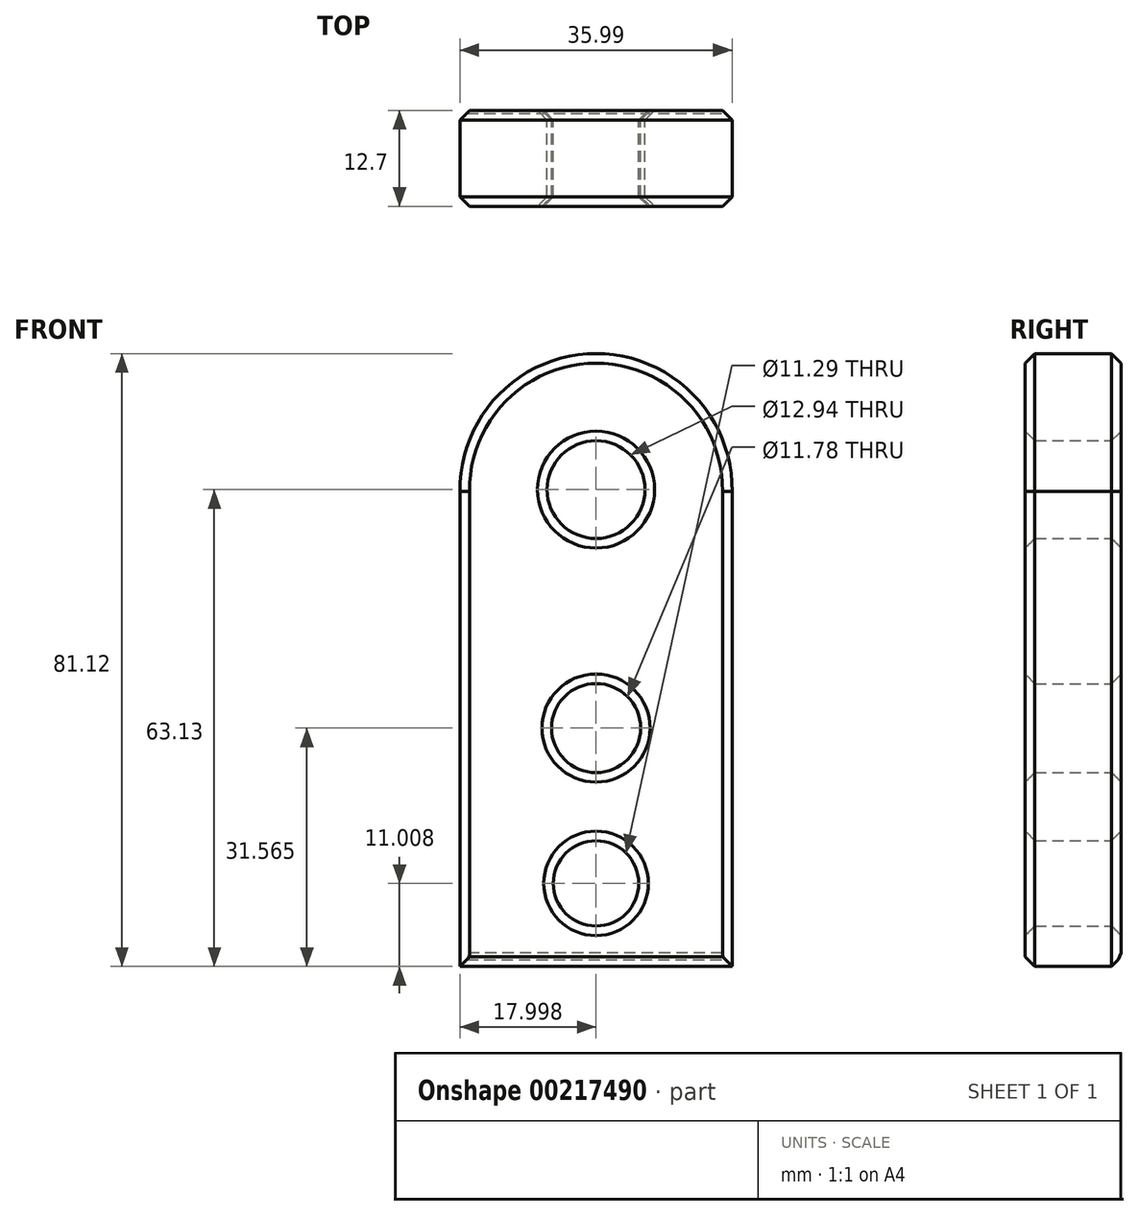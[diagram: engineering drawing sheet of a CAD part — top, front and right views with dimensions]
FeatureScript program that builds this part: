
annotation { "Feature Type Name" : "Feature", "Feature Type Description" : "" }
export const myFeature = defineFeature(function(context is Context, id is Id, definition is map)
    precondition{}
    {
        {
            var Q0;
            Q0=qCreatedBy(makeId("Front.planeOp"),FACE);
            var sketch = newSketch(context, id + "F0", { "sketchPlane" : qUnion([Q0])});
            skLineSegment(sketch, "E0.top", {"start": v(0, -62.88) * mm, "end": v(-35.98, -62.88) * mm});
            skLineSegment(sketch, "E0.left", {"start": v(0, 0) * mm, "end": v(0, -62.88) * mm});
            skLineSegment(sketch, "E0.right", {"start": v(-35.98, 0) * mm, "end": v(-35.98, -62.88) * mm});
            skArc(sketch, "E1", {"start": v(0, 0) * mm, "mid": v(-18, 18.24) * mm, "end": v(-35.98, 0) * mm});
            skPoint(sketch, "E1.third.point", {"position": v(-14.07, 17.81) * mm});
            skCircle(sketch, "E2", {"center": v(-18, 0.25) * mm, "radius": 6.47 * mm});
            skCircle(sketch, "E3", {"center": v(-18, -51.87) * mm, "radius": 5.65 * mm});
            skPoint(sketch, "E4.center.orphan", {"position": v(-18, -31.32) * mm});
            skCircle(sketch, "E5", {"center": v(-18, -31.32) * mm, "radius": 5.89 * mm});
            skPoint(sketch, "E6.trimOffspring.end.orphan", {"position": v(-18, -62.88) * mm});
            skSolve(sketch);
        }
        {
            var Q0;
            Q0 = qSketchRegion(id + "F0", true);
            extrude(context, id + "F3", {"entities" : qUnion([Q0]), "depth" : 12.7 * mm});
        }
        {
            var Q0;
            Q0=makeQuery(id+"F3.opExtrude","CAP_FACE",FACE,{"disambiguationData":[OSD([sQuery(id+"F0.wireOp",EDGE,"E0.top"),sQuery(id+"F0.wireOp",EDGE,"E0.left"),sQuery(id+"F0.wireOp",EDGE,"E0.right"),sQuery(id+"F0.wireOp",EDGE,"E1"),sQuery(id+"F0.wireOp",EDGE,"E2")])],"isStart":false});
            var Q1;
            Q1=makeQuery(id+"F3.opExtrude","CAP_EDGE",EDGE,{"disambiguationData":[OSD([sQuery(id+"F0.wireOp",EDGE,"E0.top")])],"isStart":true});
            chamfer(context, id + "F1", {"entities" : qUnion([Q0, Q1]), "width" : 1.27 * mm, "tangentPropagation" : true});
        }
        {
            var Q0;
            Q0=makeQuery(id+"F3.opExtrude","CAP_FACE",FACE,{"disambiguationData":[OSD([sQuery(id+"F0.wireOp",EDGE,"E0.top"),sQuery(id+"F0.wireOp",EDGE,"E0.left"),sQuery(id+"F0.wireOp",EDGE,"E0.right"),sQuery(id+"F0.wireOp",EDGE,"E1"),sQuery(id+"F0.wireOp",EDGE,"E2")])],"isStart":true});
            chamfer(context, id + "F2", {"entities" : qUnion([Q0]), "width" : 1.27 * mm, "tangentPropagation" : true});
        }
    });
